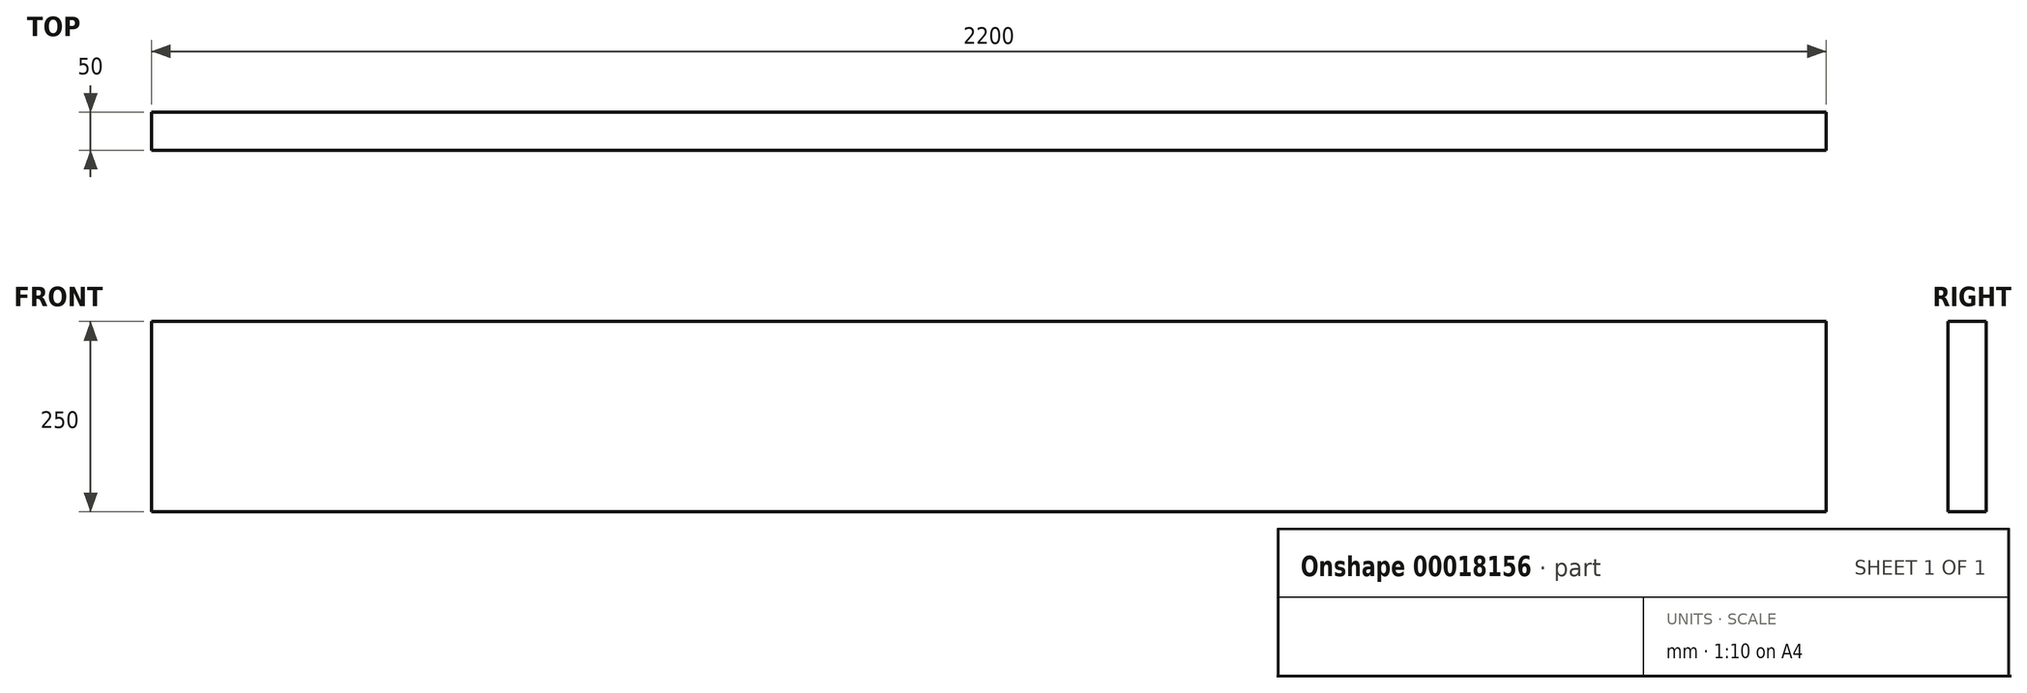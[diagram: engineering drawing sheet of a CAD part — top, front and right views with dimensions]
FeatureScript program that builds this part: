
annotation { "Feature Type Name" : "Feature", "Feature Type Description" : "" }
export const myFeature = defineFeature(function(context is Context, id is Id, definition is map)
    precondition{}
    {
        {
            var Q0;
            Q0=qCreatedBy(makeId("Right.planeOp"),FACE);
            var sketch = newSketch(context, id + "F0", { "sketchPlane" : qUnion([Q0])});
            skLineSegment(sketch, "E0.rect.bottom", {"start": v(-25, 125) * mm, "end": v(25, 125) * mm});
            skLineSegment(sketch, "E0.rect.top", {"start": v(-25, -125) * mm, "end": v(25, -125) * mm});
            skLineSegment(sketch, "E0.rect.left", {"start": v(-25, 125) * mm, "end": v(-25, -125) * mm});
            skLineSegment(sketch, "E0.rect.right", {"start": v(25, 125) * mm, "end": v(25, -125) * mm});
            skPoint(sketch, "E0.rect.middle", {"position": v(0, 0) * mm});
            skSolve(sketch);
        }
        {
            var Q0;
            Q0 = qSketchRegion(id + "F0", true);
            extrude(context, id + "F1", {"entities" : qUnion([Q0]), "endBound" : BoundingType.SYMMETRIC, "depth" : 2200 * mm});
        }
    });
